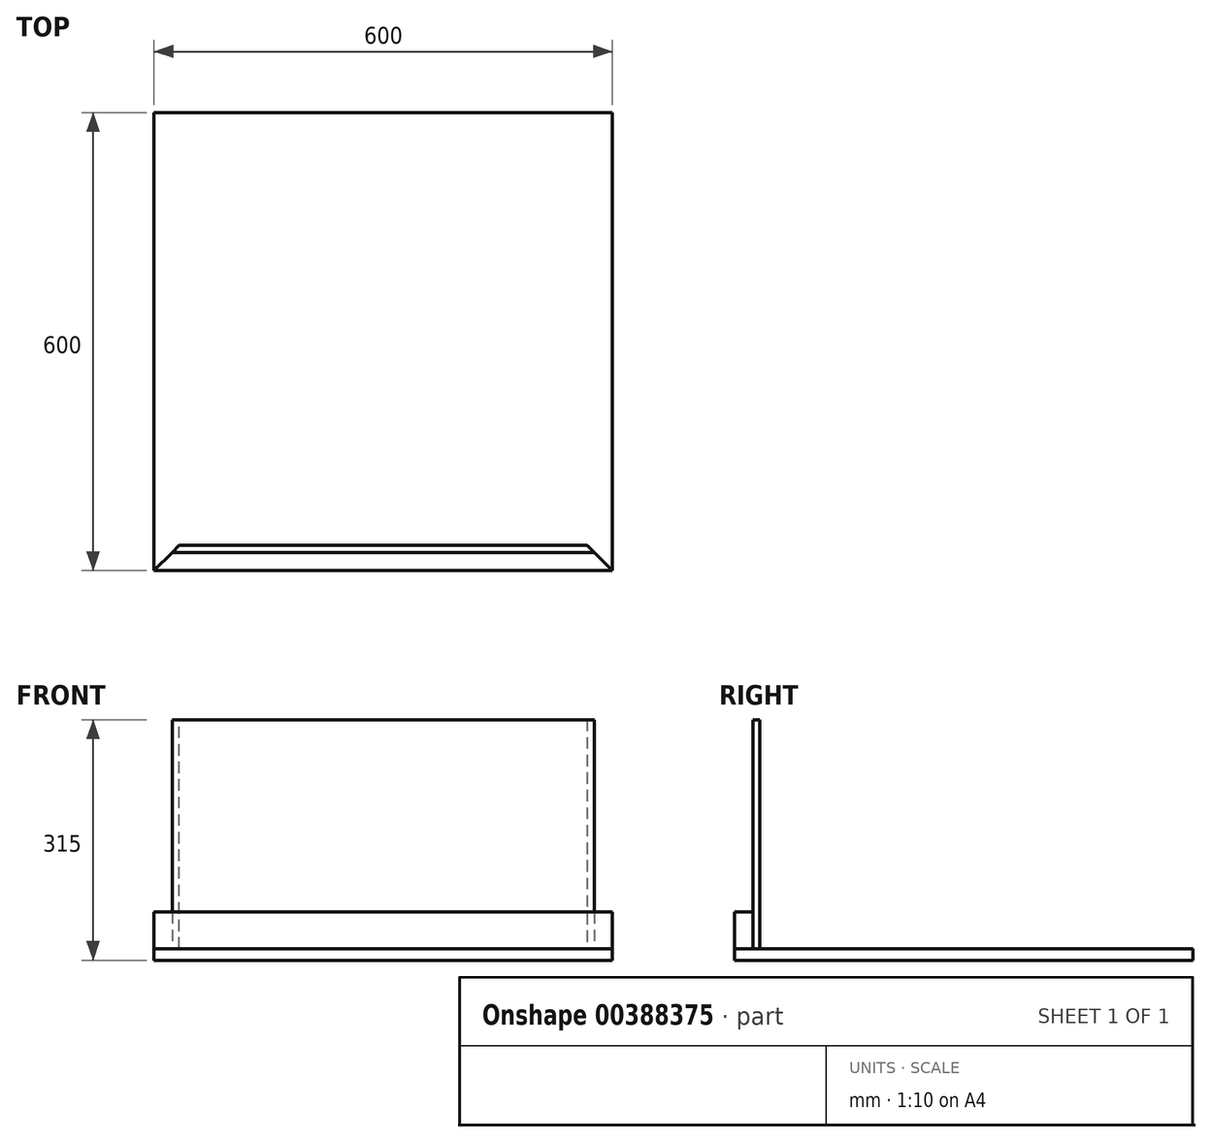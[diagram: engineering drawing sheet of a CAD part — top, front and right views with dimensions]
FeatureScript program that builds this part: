
annotation { "Feature Type Name" : "Feature", "Feature Type Description" : "" }
export const myFeature = defineFeature(function(context is Context, id is Id, definition is map)
    precondition{}
    {
        {
            var Q0;
            Q0=qCreatedBy(makeId("Top.planeOp"),FACE);
            var sketch = newSketch(context, id + "F0", { "sketchPlane" : qUnion([Q0])});
            skLineSegment(sketch, "E0.bottom", {"start": v(300, 300) * mm, "end": v(-300, 300) * mm});
            skLineSegment(sketch, "E0.top", {"start": v(300, -300) * mm, "end": v(-300, -300) * mm});
            skLineSegment(sketch, "E0.left", {"start": v(300, 300) * mm, "end": v(300, -300) * mm});
            skLineSegment(sketch, "E0.right", {"start": v(-300, 300) * mm, "end": v(-300, -300) * mm});
            skPoint(sketch, "E0.middle", {"position": v(0, 0) * mm});
            skSolve(sketch);
        }
        {
            var Q0;
            Q0 = qSketchRegion(id + "F0", true);
            extrude(context, id + "F1", {"entities" : qUnion([Q0]), "depth" : 15 * mm});
        }
        {
            var Q0;
            Q0=makeQuery(id+"F1.opExtrude","CAP_FACE",FACE,{"disambiguationData":[OSD([sQuery(id+"F0.wireOp",EDGE,"E0.bottom"),sQuery(id+"F0.wireOp",EDGE,"E0.top"),sQuery(id+"F0.wireOp",EDGE,"E0.left"),sQuery(id+"F0.wireOp",EDGE,"E0.right")])],"isStart":false});
            var sketch = newSketch(context, id + "F2", { "sketchPlane" : qUnion([Q0])});
            skLineSegment(sketch, "E1", {"start": v(-300, -300) * mm, "end": v(300, -300) * mm});
            skLineSegment(sketch, "E2", {"start": v(300, -300) * mm, "end": v(276, -276) * mm});
            skLineSegment(sketch, "E3", {"start": v(276, -276) * mm, "end": v(-276, -276) * mm});
            skLineSegment(sketch, "E4", {"start": v(-276, -276) * mm, "end": v(-300, -300) * mm});
            skCircle(sketch, "E5", {"center": v(0, 0) * mm, "radius": 15 * mm, "construction": true});
            skSolve(sketch);
        }
        {
            var Q0;
            Q0 = qSketchRegion(id + "F2", true);
            extrude(context, id + "F3", {"entities" : qUnion([Q0]), "depth" : 48 * mm});
        }
        {
            var Q0;
            Q0=makeQuery(id+"F3.opExtrude","SWEPT_FACE",FACE,{"disambiguationData":[OSD([sQuery(id+"F2.wireOp",EDGE,"E3")])]});
            var sketch = newSketch(context, id + "F4", { "sketchPlane" : qUnion([Q0])});
            skLineSegment(sketch, "E6.bottom", {"start": v(-276, 15) * mm, "end": v(276, 15) * mm});
            skLineSegment(sketch, "E6.top", {"start": v(-276, 315) * mm, "end": v(276, 315) * mm});
            skLineSegment(sketch, "E6.left", {"start": v(-276, 15) * mm, "end": v(-276, 315) * mm});
            skLineSegment(sketch, "E6.right", {"start": v(276, 15) * mm, "end": v(276, 315) * mm});
            skSolve(sketch);
        }
        {
            var Q0;
            Q0 = qSketchRegion(id + "F4", true);
            extrude(context, id + "F5", {"entities" : qUnion([Q0]), "depth" : 9 * mm});
        }
        {
            var Q0;
            Q0=makeQuery(id+"F5.opExtrude","CAP_EDGE",EDGE,{"disambiguationData":[OSD([sQuery(id+"F4.wireOp",EDGE,"E6.left")])],"isStart":false});
            var Q1;
            Q1=makeQuery(id+"F5.opExtrude","CAP_EDGE",EDGE,{"disambiguationData":[OSD([sQuery(id+"F4.wireOp",EDGE,"E6.right")])],"isStart":false});
            chamfer(context, id + "F6", {"entities" : qUnion([Q0, Q1]), "width" : 9 * mm, "tangentPropagation" : true});
        }
    });
